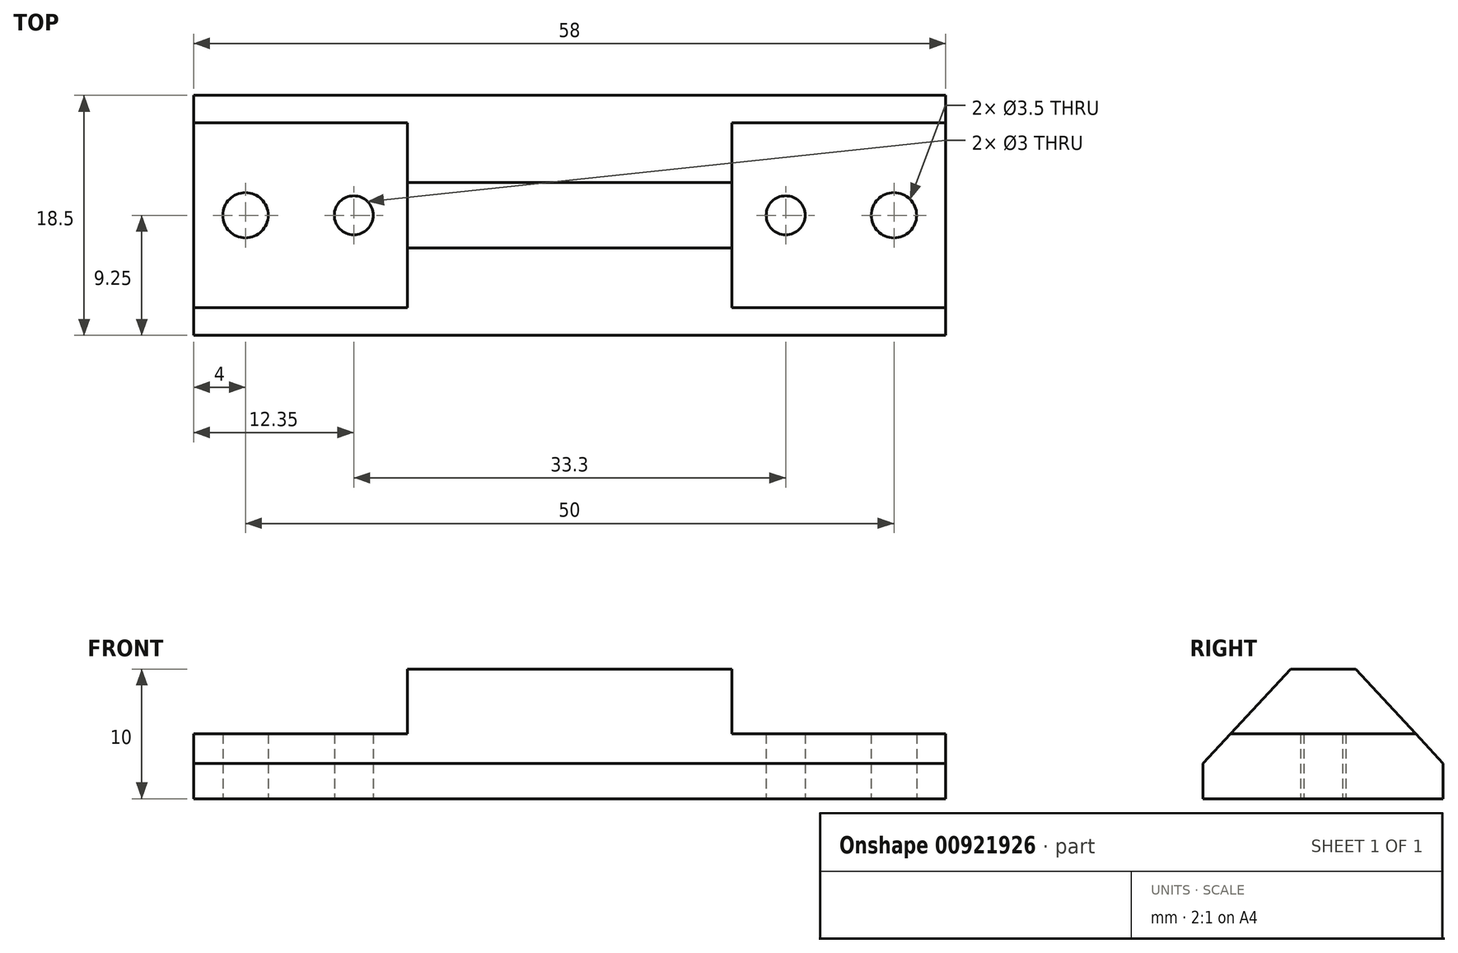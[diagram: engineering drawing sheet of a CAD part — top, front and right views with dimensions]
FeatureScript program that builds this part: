
annotation { "Feature Type Name" : "Feature", "Feature Type Description" : "" }
export const myFeature = defineFeature(function(context is Context, id is Id, definition is map)
    precondition{}
    {
        {
            var Q0;
            Q0=qCreatedBy(makeId("Top.planeOp"),FACE);
            var sketch = newSketch(context, id + "F0", { "sketchPlane" : qUnion([Q0])});
            skLineSegment(sketch, "E0.bottom", {"start": v(19, -9.25) * mm, "end": v(-19, -9.25) * mm});
            skLineSegment(sketch, "E0.top", {"start": v(19, 9.25) * mm, "end": v(-19, 9.25) * mm});
            skLineSegment(sketch, "E0.left", {"start": v(19, -9.25) * mm, "end": v(19, 9.25) * mm});
            skLineSegment(sketch, "E0.right", {"start": v(-19, -9.25) * mm, "end": v(-19, 9.25) * mm});
            skPoint(sketch, "E0.middle", {"position": v(0, 0) * mm});
            skLineSegment(sketch, "E1.bottom", {"start": v(19, -9.25) * mm, "end": v(29, -9.25) * mm});
            skLineSegment(sketch, "E1.top", {"start": v(19, 9.25) * mm, "end": v(29, 9.25) * mm});
            skLineSegment(sketch, "E1.right", {"start": v(29, -9.25) * mm, "end": v(29, 9.25) * mm});
            skLineSegment(sketch, "E2.bottom", {"start": v(-19, -9.25) * mm, "end": v(-29, -9.25) * mm});
            skLineSegment(sketch, "E2.top", {"start": v(-19, 9.25) * mm, "end": v(-29, 9.25) * mm});
            skLineSegment(sketch, "E2.right", {"start": v(-29, -9.25) * mm, "end": v(-29, 9.25) * mm});
            skCircle(sketch, "E3", {"center": v(-25, 0) * mm, "radius": 1.75 * mm});
            skPoint(sketch, "E3.centerSnap0", {"position": v(-29, 0) * mm});
            skCircle(sketch, "E4", {"center": v(25, 0) * mm, "radius": 1.75 * mm});
            skPoint(sketch, "E4.centerSnap0", {"position": v(29, 0) * mm});
            skCircle(sketch, "E5", {"center": v(-16.65, 0) * mm, "radius": 1.5 * mm});
            skCircle(sketch, "E6", {"center": v(16.65, 0) * mm, "radius": 1.5 * mm});
            skSolve(sketch);
        }
        {
            var Q0;
            Q0=qSketchRegion(id+"F0",true);
            extrude(context, id + "F1", {"entities" : qUnion([Q0]), "depth" : 10 * mm, "offsetDistance" : 25 * mm});
        }
        {
            var Q0;
            Q0=makeQuery(id+"F1.opExtrude","SWEPT_FACE",FACE,{"disambiguationData":[OSD([sQuery(id+"F0.wireOp",EDGE,"E1.right")])]});
            var sketch = newSketch(context, id + "F2", { "sketchPlane" : qUnion([Q0])});
            skLineSegment(sketch, "E7", {"start": v(-9.25, 2.72) * mm, "end": v(0, 12.72) * mm});
            skLineSegment(sketch, "E8", {"start": v(0, 12.72) * mm, "end": v(9.25, 2.72) * mm});
            skLineSegment(sketch, "E9", {"start": v(-9.25, 2.72) * mm, "end": v(9.25, 2.72) * mm});
            skLineSegment(sketch, "E10", {"start": v(-4.62, 7.72) * mm, "end": v(0, 2.72) * mm});
            skLineSegment(sketch, "E11", {"start": v(0, 2.72) * mm, "end": v(4.62, 7.72) * mm});
            skLineSegment(sketch, "E12", {"start": v(4.62, 7.72) * mm, "end": v(-4.62, 7.72) * mm});
            skSolve(sketch);
        }
        {
            var Q0;
            {var subQ0=sQuery(id+"F2.wireOp",EDGE,"E7");var subQ1=sQuery(id+"F0.wireOp",EDGE,"E1.right");var subQ5=makeQuery(id+"F1.opExtrude","CAP_EDGE",EDGE,{"disambiguationData":[OSD([subQ1])],"isStart":false});var subQ6=makeQuery(id+"F2.imprint","INTERSECT",VERTEX,{"derivedFrom":[subQ5,subQ0]});Q0=makeQuery(id+"F2.imprint","IMPRINT",FACE,{"disambiguationData":[TD([[makeQuery(id+"F2.imprint","IMPRINT",EDGE,{"disambiguationData":[TD([[subQ6,1.0]])],"derivedFrom":subQ0}),1.0]])]});}
            var Q1;
            {var subQ0=sQuery(id+"F2.wireOp",EDGE,"E8");var subQ2=sQuery(id+"F0.wireOp",EDGE,"E1.right");var subQ3=makeQuery(id+"F1.opExtrude","CAP_EDGE",EDGE,{"disambiguationData":[OSD([subQ2])],"isStart":false});var subQ4=makeQuery(id+"F2.imprint","INTERSECT",VERTEX,{"derivedFrom":[subQ3,subQ0]});Q1=makeQuery(id+"F2.imprint","IMPRINT",FACE,{"disambiguationData":[TD([[makeQuery(id+"F2.imprint","IMPRINT",EDGE,{"disambiguationData":[TD([[subQ4,-1.0]])],"derivedFrom":subQ0}),1.0]])]});}
            extrude(context, id + "F3", {"entities" : qUnion([Q0, Q1]), "operationType" : NewBodyOperationType.REMOVE, "endBound" : BoundingType.THROUGH_ALL, "oppositeDirection" : true, "depth" : 25 * mm, "offsetDistance" : 25 * mm});
        }
        {
            var Q0;
            Q0=qCreatedBy(makeId("Front.planeOp"),FACE);
            var sketch = newSketch(context, id + "F4", { "sketchPlane" : qUnion([Q0])});
            skLineSegment(sketch, "E13", {"start": v(0, 0) * mm, "end": v(29, 0) * mm, "construction": true});
            skLineSegment(sketch, "E14", {"start": v(29, 0) * mm, "end": v(12.5, 0) * mm});
            skLineSegment(sketch, "E15", {"start": v(0, 0) * mm, "end": v(-29, 0) * mm, "construction": true});
            skLineSegment(sketch, "E16", {"start": v(-29, 0) * mm, "end": v(-12.5, 0) * mm});
            skLineSegment(sketch, "E17", {"start": v(-12.5, 0) * mm, "end": v(-12.5, 5) * mm});
            skLineSegment(sketch, "E18", {"start": v(-12.5, 5) * mm, "end": v(-29, 5) * mm});
            skLineSegment(sketch, "E19", {"start": v(-29, 5) * mm, "end": v(-29, 0) * mm});
            skLineSegment(sketch, "E20", {"start": v(12.5, 0) * mm, "end": v(12.5, 5) * mm});
            skLineSegment(sketch, "E21", {"start": v(12.5, 5) * mm, "end": v(29, 5) * mm});
            skLineSegment(sketch, "E22", {"start": v(29, 5) * mm, "end": v(29, 0) * mm});
            skLineSegment(sketch, "E23.bottom", {"start": v(-29, 5) * mm, "end": v(29, 5) * mm});
            skLineSegment(sketch, "E23.top", {"start": v(-29, 17) * mm, "end": v(29, 17) * mm});
            skLineSegment(sketch, "E23.left", {"start": v(-29, 5) * mm, "end": v(-29, 17) * mm});
            skLineSegment(sketch, "E23.right", {"start": v(29, 5) * mm, "end": v(29, 17) * mm});
            skLineSegment(sketch, "E24", {"start": v(-12.5, 5) * mm, "end": v(-12.5, 17) * mm});
            skLineSegment(sketch, "E25", {"start": v(12.5, 5) * mm, "end": v(12.5, 17) * mm});
            skSolve(sketch);
        }
        {
            var Q0;
            Q0=makeQuery(id+"F4.imprint","IMPRINT",FACE,{"disambiguationData":[TD([[makeQuery(id+"F4.imprint","IMPRINT",EDGE,{"derivedFrom":sQuery(id+"F4.wireOp",EDGE,"E18")}),-1.0]])]});
            var Q1;
            Q1=makeQuery(id+"F4.imprint","IMPRINT",FACE,{"disambiguationData":[TD([[makeQuery(id+"F4.imprint","IMPRINT",EDGE,{"derivedFrom":sQuery(id+"F4.wireOp",EDGE,"E21")}),1.0]])]});
            extrude(context, id + "F5", {"entities" : qUnion([Q0, Q1]), "operationType" : NewBodyOperationType.REMOVE, "depth" : 25 * mm, "offsetDistance" : 25 * mm, "hasSecondDirection" : true, "secondDirectionOppositeDirection" : true, "secondDirectionDepth" : 25 * mm});
        }
    });
